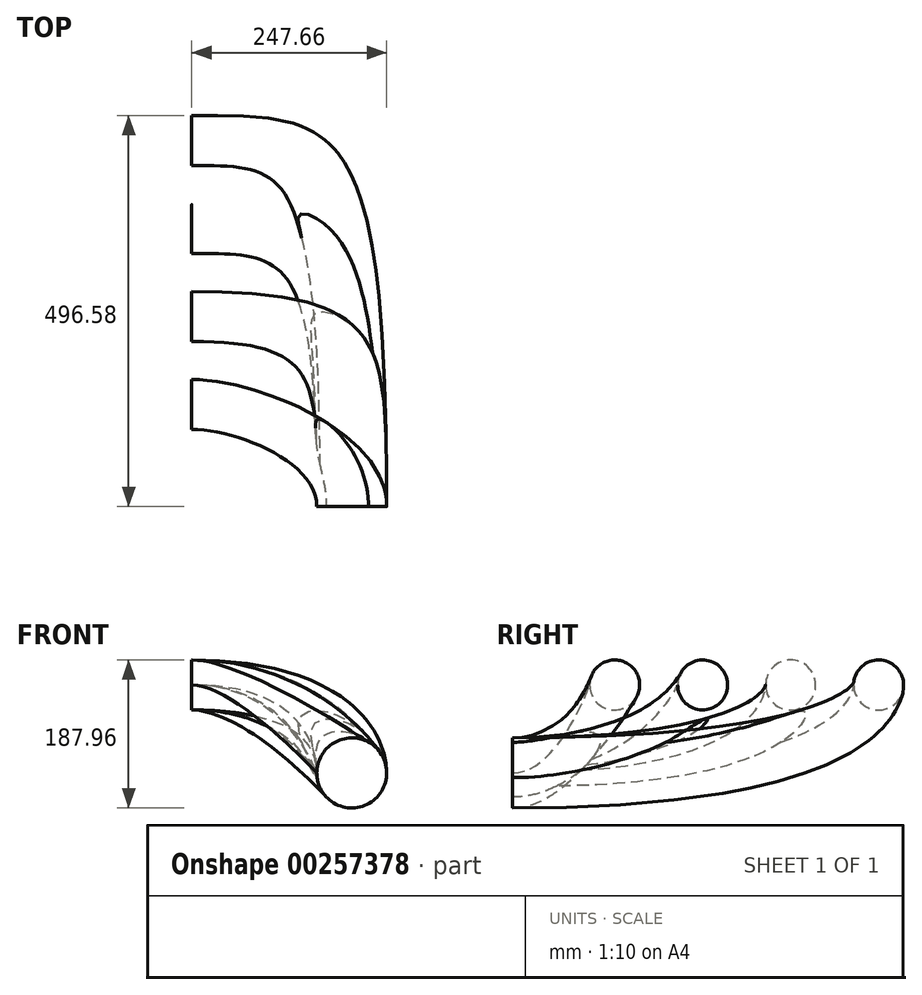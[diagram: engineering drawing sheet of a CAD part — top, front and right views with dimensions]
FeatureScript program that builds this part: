
annotation { "Feature Type Name" : "Feature", "Feature Type Description" : "" }
export const myFeature = defineFeature(function(context is Context, id is Id, definition is map)
    precondition{}
    {
        {
            var Q0;
            Q0=qCreatedBy(makeId("Right.planeOp"),FACE);
            cPlane(context, id + "F0", {"entities" : qUnion([Q0]), "cplaneType" : CPlaneType.OFFSET, "offset" : 203.2 * mm, "oppositeDirection" : true, "width" : 152.4 * mm, "height" : 152.4 * mm});
        }
        {
            var Q0;
            Q0=qCreatedBy(makeId("Top.planeOp"),FACE);
            cPlane(context, id + "F1", {"entities" : qUnion([Q0]), "cplaneType" : CPlaneType.OFFSET, "offset" : 111.76 * mm, "width" : 152.4 * mm, "height" : 152.4 * mm});
        }
        {
            var Q0;
            Q0=qCreatedBy(makeId("Front.planeOp"),FACE);
            var sketch = newSketch(context, id + "F2", { "sketchPlane" : qUnion([Q0])});
            skCircle(sketch, "E0", {"center": v(0, 0) * mm, "radius": 44.45 * mm});
            skSolve(sketch);
        }
        {
            var Q0;
            Q0=qCreatedBy(id+"F0.planeOp",FACE);
            var sketch = newSketch(context, id + "F3", { "sketchPlane" : qUnion([Q0])});
            skCircle(sketch, "E1", {"center": v(129.54, 111.76) * mm, "radius": 31.75 * mm});
            skCircle(sketch, "E2.1.0.0", {"center": v(241.3, 111.76) * mm, "radius": 31.75 * mm});
            skCircle(sketch, "E2.2.0.0", {"center": v(353.06, 111.76) * mm, "radius": 31.75 * mm});
            skCircle(sketch, "E2.3.0.0", {"center": v(464.82, 111.76) * mm, "radius": 31.75 * mm});
            skLineSegment(sketch, "E2.direction1", {"start": v(129.54, 111.76) * mm, "end": v(241.3, 111.76) * mm, "construction": true});
            skSolve(sketch);
        }
        {
            var Q0;
            Q0=qCreatedBy(makeId("Top.planeOp"),FACE);
            var sketch = newSketch(context, id + "F4", { "sketchPlane" : qUnion([Q0])});
            skLineSegment(sketch, "E3", {"start": v(0, 0) * mm, "end": v(0, -195.45) * mm, "construction": true});
            skSolve(sketch);
        }
        {
            var Q0;
            Q0=qCreatedBy(id+"F1.planeOp",FACE);
            var sketch = newSketch(context, id + "F5", { "sketchPlane" : qUnion([Q0])});
            skLineSegment(sketch, "E4.0", {"start": v(0, 0) * mm, "end": v(0, -195.45) * mm});
            skLineSegment(sketch, "E5.0", {"start": v(-203.2, 161.3) * mm, "end": v(-203.2, 97.8) * mm});
            skLineSegment(sketch, "E6.0", {"start": v(-203.2, 273.05) * mm, "end": v(-203.2, 209.55) * mm});
            skLineSegment(sketch, "E7.0", {"start": v(-203.2, 384.81) * mm, "end": v(-203.2, 321.31) * mm});
            skLineSegment(sketch, "E8.0", {"start": v(-203.2, 496.57) * mm, "end": v(-203.2, 433.07) * mm});
            skLineSegment(sketch, "E9", {"start": v(-203.2, 97.8) * mm, "end": v(-177.8, 97.8) * mm});
            skLineSegment(sketch, "E10", {"start": v(-203.2, 97.8) * mm, "end": v(-203.2, 209.55) * mm});
            skPoint(sketch, "E11", {"position": v(-190.5, 97.8) * mm});
            skLineSegment(sketch, "E12.0.1.0", {"start": v(-203.2, 209.55) * mm, "end": v(-177.8, 209.55) * mm});
            skLineSegment(sketch, "E12.0.2.0", {"start": v(-203.2, 321.31) * mm, "end": v(-177.8, 321.31) * mm});
            skLineSegment(sketch, "E12.0.3.0", {"start": v(-203.2, 433.07) * mm, "end": v(-177.8, 433.07) * mm});
            skLineSegment(sketch, "E12.direction1", {"start": v(-203.2, 97.8) * mm, "end": v(-177.8, 97.8) * mm, "construction": true});
            skLineSegment(sketch, "E12.direction2", {"start": v(-203.2, 97.8) * mm, "end": v(-203.2, 209.55) * mm, "construction": true});
            skPoint(sketch, "E13", {"position": v(-190.5, 209.55) * mm});
            skPoint(sketch, "E14", {"position": v(-190.5, 321.31) * mm});
            skPoint(sketch, "E15", {"position": v(-190.5, 433.07) * mm});
            skSolve(sketch);
        }
        {
            var Q0;
            Q0=qCreatedBy(makeId("Top.planeOp"),FACE);
            var sketch = newSketch(context, id + "F6", { "sketchPlane" : qUnion([Q0])});
            skLineSegment(sketch, "E16.0", {"start": v(44.45, 0) * mm, "end": v(-44.45, 0) * mm, "construction": true});
            skLineSegment(sketch, "E17", {"start": v(44.45, 0) * mm, "end": v(-44.45, 0) * mm});
            skLineSegment(sketch, "E18", {"start": v(-44.45, 0) * mm, "end": v(-44.45, 25.4) * mm});
            skPoint(sketch, "E19", {"position": v(-44.45, 8.03) * mm});
            skSolve(sketch);
        }
        {
            var Q0;
            Q0=qCreatedBy(makeId("Front.planeOp"),FACE);
            cPlane(context, id + "F7", {"entities" : qUnion([Q0]), "cplaneType" : CPlaneType.OFFSET, "offset" : 76.2 * mm, "oppositeDirection" : true, "width" : 152.4 * mm, "height" : 152.4 * mm});
        }
        {
            var Q0;
            Q0=qCreatedBy(makeId("Right.planeOp"),FACE);
            cPlane(context, id + "F8", {"entities" : qUnion([Q0]), "cplaneType" : CPlaneType.OFFSET, "offset" : 76.2 * mm, "oppositeDirection" : true, "width" : 152.4 * mm, "height" : 152.4 * mm});
        }
        {
            var Q0;
            Q0=makeQuery(id+"F2.imprint","IMPRINT",FACE,{"disambiguationData":[TD([[makeQuery(id+"F2.imprint","IMPRINT",EDGE,{"derivedFrom":sQuery(id+"F2.wireOp",EDGE,"E0")}),1.0]])]});
            var Q1;
            Q1=makeQuery(id+"F3.imprint","IMPRINT",FACE,{"disambiguationData":[TD([[makeQuery(id+"F3.imprint","IMPRINT",EDGE,{"derivedFrom":sQuery(id+"F3.wireOp",EDGE,"E1")}),1.0]])]});
            var Q2;
            Q2=sQuery(id+"F5.wireOp",VERTEX,"E12.direction1.start");
            var Q3;
            Q3=sQuery(id+"F6.wireOp",VERTEX,"E18.start");
            loft(context, id + "F9", {"startCondition" : LoftEndDerivativeType.NORMAL_TO_PROFILE, "startMagnitude" : 1.6, "endCondition" : LoftEndDerivativeType.NORMAL_TO_PROFILE, "endMagnitude" : 1, "sheetProfilesArray" : [{ "sheetProfileEntities" : qUnion([Q0]) }, { "sheetProfileEntities" : qUnion([Q1]) }], "matchConnections" : true, "connections" : [{ "connectionEntities" : qUnion([Q2, Q3]), "connectionEdgeQueries" : qUnion([]), "connectionEdgeParameters" : [] }]});
        }
        {
            var Q0;
            Q0=makeQuery(id+"F2.imprint","IMPRINT",FACE,{"disambiguationData":[TD([[makeQuery(id+"F2.imprint","IMPRINT",EDGE,{"derivedFrom":sQuery(id+"F2.wireOp",EDGE,"E0")}),1.0]])]});
            var Q1;
            Q1=makeQuery(id+"F3.imprint","IMPRINT",FACE,{"disambiguationData":[TD([[makeQuery(id+"F3.imprint","IMPRINT",EDGE,{"derivedFrom":sQuery(id+"F3.wireOp",EDGE,"E2.1.0.0")}),1.0]])]});
            var Q2;
            Q2=sQuery(id+"F5.wireOp",VERTEX,"E6.0.end");
            var Q3;
            Q3=sQuery(id+"F6.wireOp",VERTEX,"E18.start");
            loft(context, id + "F10", {"operationType" : NewBodyOperationType.ADD, "startCondition" : LoftEndDerivativeType.NORMAL_TO_PROFILE, "startMagnitude" : 2.2, "endCondition" : LoftEndDerivativeType.NORMAL_TO_PROFILE, "endMagnitude" : 2.9, "sheetProfilesArray" : [{ "sheetProfileEntities" : qUnion([Q0]) }, { "sheetProfileEntities" : qUnion([Q1]) }], "matchConnections" : true, "connections" : [{ "connectionEntities" : qUnion([Q2, Q3]), "connectionEdgeQueries" : qUnion([]), "connectionEdgeParameters" : [] }]});
        }
        {
            var Q0;
            Q0=makeQuery(id+"F2.imprint","IMPRINT",FACE,{"disambiguationData":[TD([[makeQuery(id+"F2.imprint","IMPRINT",EDGE,{"derivedFrom":sQuery(id+"F2.wireOp",EDGE,"E0")}),1.0]])]});
            var Q1;
            Q1=makeQuery(id+"F3.imprint","IMPRINT",FACE,{"disambiguationData":[TD([[makeQuery(id+"F3.imprint","IMPRINT",EDGE,{"derivedFrom":sQuery(id+"F3.wireOp",EDGE,"E2.2.0.0")}),1.0]])]});
            var Q2;
            Q2=sQuery(id+"F5.wireOp",VERTEX,"E7.0.end");
            var Q3;
            Q3=sQuery(id+"F6.wireOp",VERTEX,"E18.start");
            loft(context, id + "F11", {"operationType" : NewBodyOperationType.ADD, "startCondition" : LoftEndDerivativeType.NORMAL_TO_PROFILE, "startMagnitude" : 3, "endCondition" : LoftEndDerivativeType.NORMAL_TO_PROFILE, "endMagnitude" : 2, "sheetProfilesArray" : [{ "sheetProfileEntities" : qUnion([Q0]) }, { "sheetProfileEntities" : qUnion([Q1]) }], "matchConnections" : true, "connections" : [{ "connectionEntities" : qUnion([Q2, Q3]), "connectionEdgeQueries" : qUnion([]), "connectionEdgeParameters" : [] }]});
        }
        {
            var Q0;
            Q0=makeQuery(id+"F2.imprint","IMPRINT",FACE,{"disambiguationData":[TD([[makeQuery(id+"F2.imprint","IMPRINT",EDGE,{"derivedFrom":sQuery(id+"F2.wireOp",EDGE,"E0")}),1.0]])]});
            var Q1;
            Q1=makeQuery(id+"F3.imprint","IMPRINT",FACE,{"disambiguationData":[TD([[makeQuery(id+"F3.imprint","IMPRINT",EDGE,{"derivedFrom":sQuery(id+"F3.wireOp",EDGE,"E2.3.0.0")}),1.0]])]});
            var Q2;
            Q2=sQuery(id+"F5.wireOp",VERTEX,"E12.0.3.0.start");
            var Q3;
            Q3=sQuery(id+"F6.wireOp",VERTEX,"E18.start");
            loft(context, id + "F12", {"operationType" : NewBodyOperationType.ADD, "startCondition" : LoftEndDerivativeType.NORMAL_TO_PROFILE, "startMagnitude" : 3, "endCondition" : LoftEndDerivativeType.NORMAL_TO_PROFILE, "endMagnitude" : 2, "sheetProfilesArray" : [{ "sheetProfileEntities" : qUnion([Q0]) }, { "sheetProfileEntities" : qUnion([Q1]) }], "matchConnections" : true, "connections" : [{ "connectionEntities" : qUnion([Q2, Q3]), "connectionEdgeQueries" : qUnion([]), "connectionEdgeParameters" : [] }]});
        }
    });
